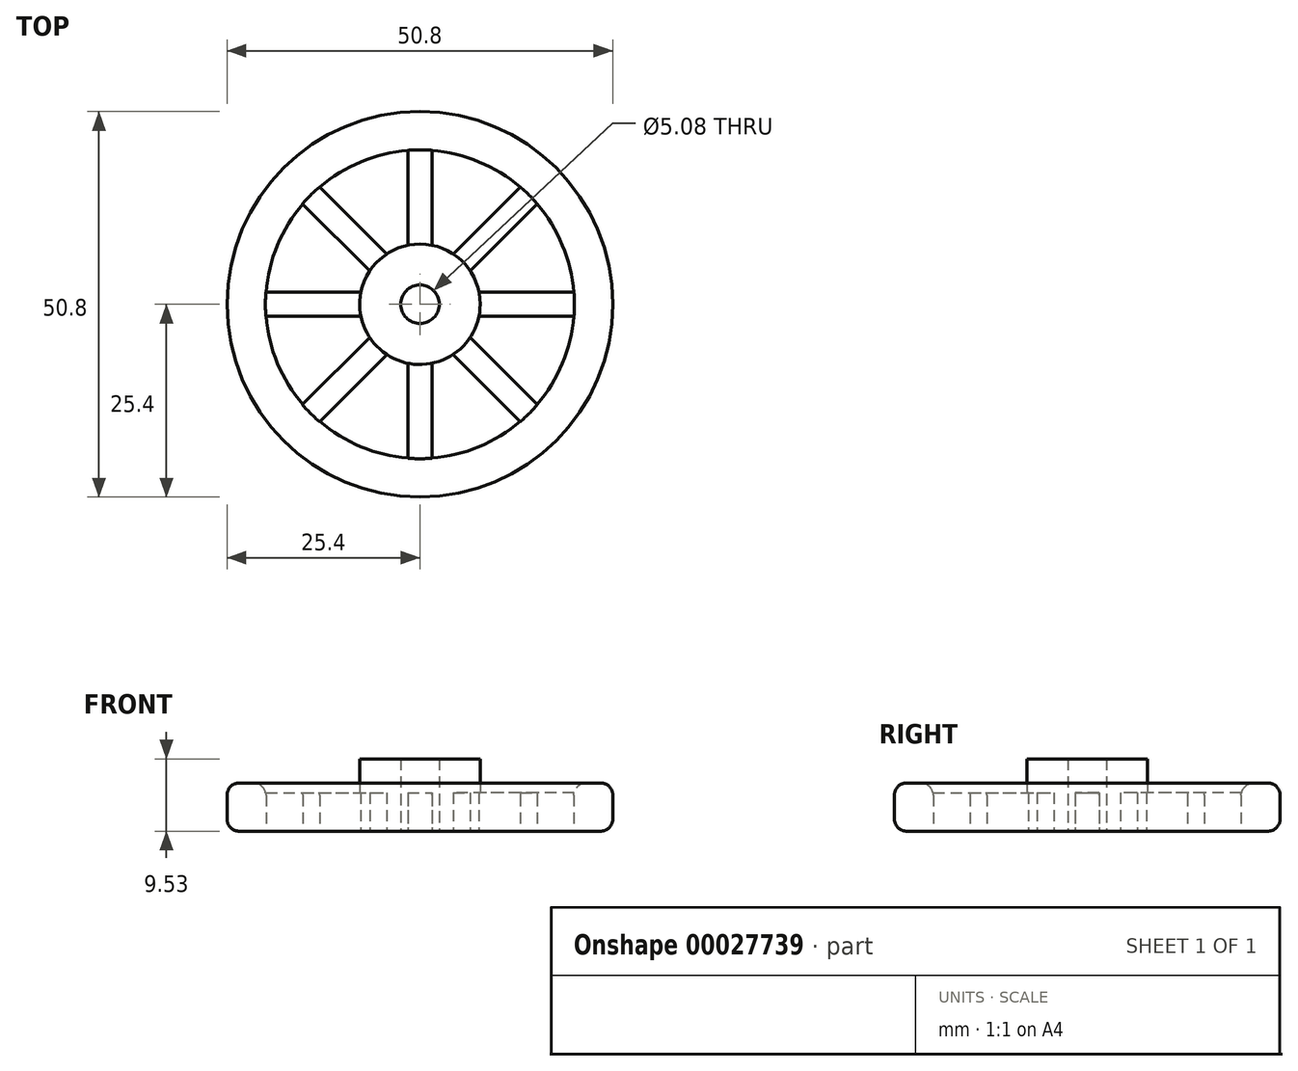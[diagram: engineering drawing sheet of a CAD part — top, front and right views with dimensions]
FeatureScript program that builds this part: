
annotation { "Feature Type Name" : "Feature", "Feature Type Description" : "" }
export const myFeature = defineFeature(function(context is Context, id is Id, definition is map)
    precondition{}
    {
        {
            var Q0;
            Q0=qCreatedBy(makeId("Top.planeOp"),FACE);
            var sketch = newSketch(context, id + "F0", { "sketchPlane" : qUnion([Q0])});
            skCircle(sketch, "E0", {"center": v(0, 0) * mm, "radius": 25.4 * mm});
            skCircle(sketch, "E1", {"center": v(0, 0) * mm, "radius": 20.32 * mm});
            skCircle(sketch, "E2", {"center": v(0, 0) * mm, "radius": 7.94 * mm});
            skCircle(sketch, "E3", {"center": v(0, 0) * mm, "radius": 2.54 * mm});
            skSolve(sketch);
        }
        {
            var Q0;
            Q0=makeQuery(id+"F0.imprint","IMPRINT",FACE,{"disambiguationData":[TD([[makeQuery(id+"F0.imprint","IMPRINT",EDGE,{"derivedFrom":sQuery(id+"F0.wireOp",EDGE,"E0")}),1.0]])]});
            extrude(context, id + "F1", {"entities" : qUnion([Q0]), "depth" : 6.35 * mm});
        }
        {
            var Q0;
            Q0=qCreatedBy(makeId("Top.planeOp"),FACE);
            var sketch = newSketch(context, id + "F2", { "sketchPlane" : qUnion([Q0])});
            skLineSegment(sketch, "E4.bottom", {"start": v(-1.59, 20.32) * mm, "end": v(1.59, 20.32) * mm});
            skLineSegment(sketch, "E4.top", {"start": v(-1.59, 0) * mm, "end": v(1.59, 0) * mm});
            skLineSegment(sketch, "E4.left", {"start": v(1.59, 20.32) * mm, "end": v(1.59, 0) * mm});
            skLineSegment(sketch, "E4.right", {"start": v(-1.59, 20.32) * mm, "end": v(-1.59, 0) * mm});
            skSolve(sketch);
        }
        {
            var Q0;
            Q0 = qSketchRegion(id + "F2", true);
            extrude(context, id + "F3", {"entities" : qUnion([Q0]), "depth" : 5.08 * mm});
        }
        {
            var Q0;
            Q0=qCreatedBy(makeId("Front.planeOp"),FACE);
            var sketch = newSketch(context, id + "F4", { "sketchPlane" : qUnion([Q0])});
            skLineSegment(sketch, "E5", {"start": v(0, 0) * mm, "end": v(0, 15.84) * mm, "construction": true});
            skSolve(sketch);
        }
        {
            var Q0;
            Q0=makeQuery(id+"F3.opExtrude","SWEPT_BODY",BODY,{"disambiguationData":[OSD([sQuery(id+"F2.wireOp",EDGE,"E4.bottom"),sQuery(id+"F2.wireOp",EDGE,"E4.top"),sQuery(id+"F2.wireOp",EDGE,"E4.left"),sQuery(id+"F2.wireOp",EDGE,"E4.right")])]});
            var Q1;
            Q1=sQuery(id+"F4.wireOp",EDGE,"E5");
            circularPattern(context, id + "F5", {"operationType" : NewBodyOperationType.ADD, "entities" : qUnion([Q0]), "axis" : qUnion([Q1]), "angle" : 360 * degree, "instanceCount" : 8, "equalSpace" : true});
        }
        {
            var Q0;
            Q0=makeQuery(id+"F0.imprint","IMPRINT",FACE,{"disambiguationData":[TD([[makeQuery(id+"F0.imprint","IMPRINT",EDGE,{"derivedFrom":sQuery(id+"F0.wireOp",EDGE,"E3")}),1.0]])]});
            var Q1;
            Q1=makeQuery(id+"F0.imprint","IMPRINT",FACE,{"disambiguationData":[TD([[makeQuery(id+"F0.imprint","IMPRINT",EDGE,{"derivedFrom":sQuery(id+"F0.wireOp",EDGE,"E2")}),1.0]])]});
            extrude(context, id + "F6", {"entities" : qUnion([Q0, Q1]), "operationType" : NewBodyOperationType.ADD, "depth" : 9.52 * mm});
        }
        {
            var Q0;
            Q0=makeQuery(id+"F0.imprint","IMPRINT",FACE,{"disambiguationData":[TD([[makeQuery(id+"F0.imprint","IMPRINT",EDGE,{"derivedFrom":sQuery(id+"F0.wireOp",EDGE,"E3")}),1.0]])]});
            var Q1;
            Q1=sQuery(id+"F0.wireOp",EDGE,"E3");
            extrude(context, id + "F7", {"entities" : qUnion([Q0]), "operationType" : NewBodyOperationType.REMOVE, "surfaceEntities" : qUnion([Q1]), "depth" : 25.4 * mm});
        }
        {
            var Q0;
            Q0=makeQuery(id+"F1.opExtrude","CAP_EDGE",EDGE,{"disambiguationData":[OSD([sQuery(id+"F0.wireOp",EDGE,"E0")])],"isStart":false});
            var Q1;
            Q1=makeQuery(id+"F1.opExtrude","SWEPT_FACE",FACE,{"disambiguationData":[OSD([sQuery(id+"F0.wireOp",EDGE,"E0")])]});
            var Q2;
            Q2=makeQuery(id+"F1.opExtrude","CAP_EDGE",EDGE,{"disambiguationData":[OSD([sQuery(id+"F0.wireOp",EDGE,"E1")])],"isStart":false});
            fillet(context, id + "F8", {"entities" : qUnion([Q0, Q1, Q2]), "radius" : 1.59 * mm, "tangentPropagation" : true, "allowEdgeOverflow" : false});
        }
    });
